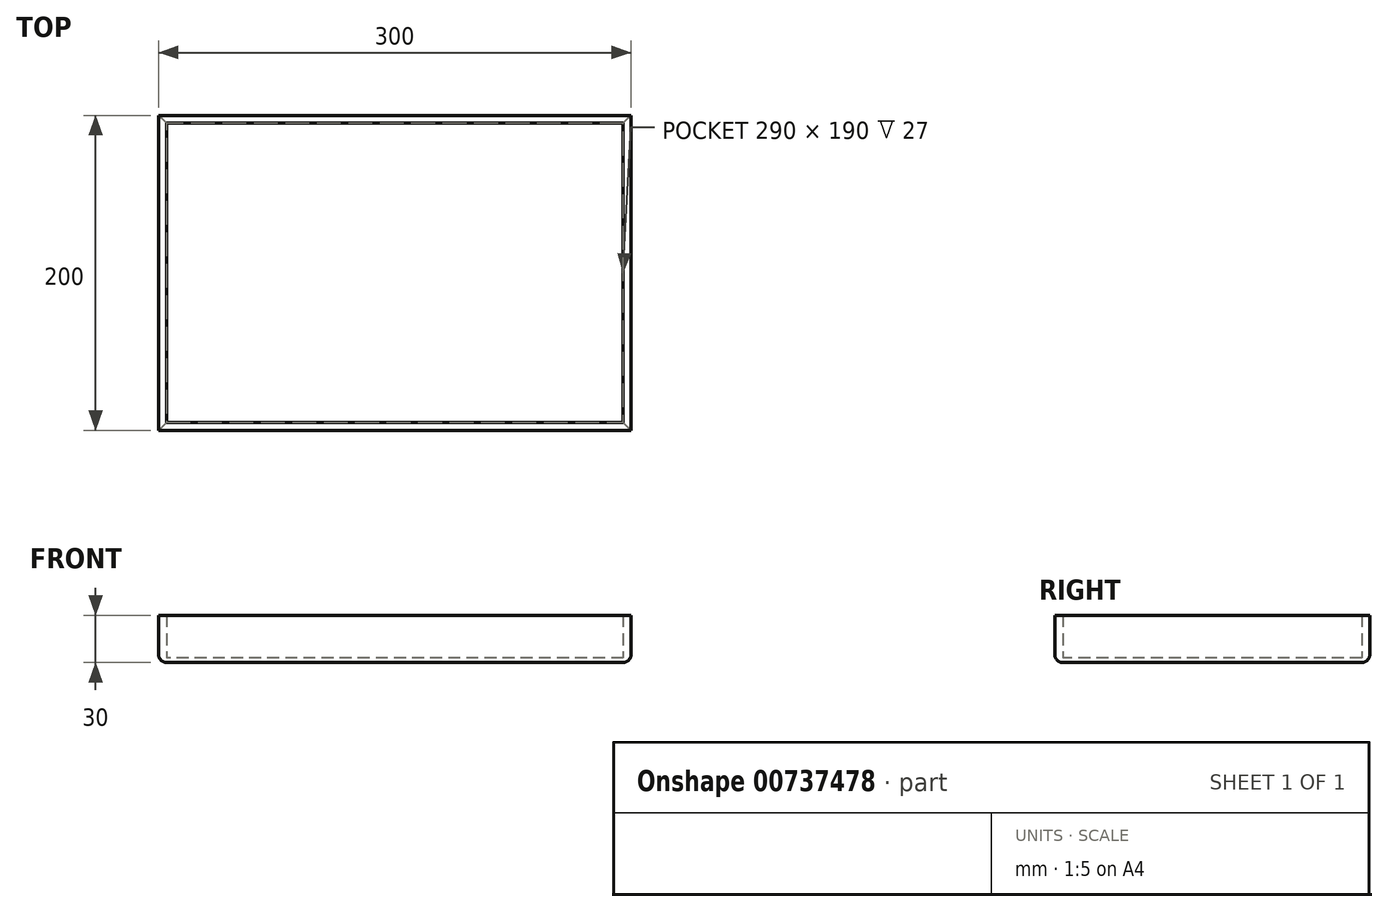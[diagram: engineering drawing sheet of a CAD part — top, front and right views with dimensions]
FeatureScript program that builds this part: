
annotation { "Feature Type Name" : "Feature", "Feature Type Description" : "" }
export const myFeature = defineFeature(function(context is Context, id is Id, definition is map)
    precondition{}
    {
        {
            var Q0;
            Q0=qCreatedBy(makeId("Top.planeOp"),FACE);
            var sketch = newSketch(context, id + "F0", { "sketchPlane" : qUnion([Q0])});
            skLineSegment(sketch, "E0.bottom", {"start": v(150, 100) * mm, "end": v(-150, 100) * mm});
            skLineSegment(sketch, "E0.top", {"start": v(150, -100) * mm, "end": v(-150, -100) * mm});
            skLineSegment(sketch, "E0.left", {"start": v(150, 100) * mm, "end": v(150, -100) * mm});
            skLineSegment(sketch, "E0.right", {"start": v(-150, 100) * mm, "end": v(-150, -100) * mm});
            skPoint(sketch, "E0.middle", {"position": v(0, 0) * mm});
            skLineSegment(sketch, "E1.bottom", {"start": v(145, 95) * mm, "end": v(-145, 95) * mm});
            skLineSegment(sketch, "E1.top", {"start": v(145, -95) * mm, "end": v(-145, -95) * mm});
            skLineSegment(sketch, "E1.left", {"start": v(145, 95) * mm, "end": v(145, -95) * mm});
            skLineSegment(sketch, "E1.right", {"start": v(-145, 95) * mm, "end": v(-145, -95) * mm});
            skLineSegment(sketch, "E2.bottom", {"start": v(147.5, 97.5) * mm, "end": v(-147.5, 97.5) * mm});
            skLineSegment(sketch, "E2.top", {"start": v(147.5, -97.5) * mm, "end": v(-147.5, -97.5) * mm});
            skLineSegment(sketch, "E2.left", {"start": v(147.5, 97.5) * mm, "end": v(147.5, -97.5) * mm});
            skLineSegment(sketch, "E2.right", {"start": v(-147.5, 97.5) * mm, "end": v(-147.5, -97.5) * mm});
            skSolve(sketch);
        }
        {
            var Q0;
            Q0=makeQuery(id+"F0.imprint","IMPRINT",FACE,{"disambiguationData":[TD([[makeQuery(id+"F0.imprint","IMPRINT",EDGE,{"derivedFrom":sQuery(id+"F0.wireOp",EDGE,"E0.bottom")}),1.0]])]});
            var Q1;
            Q1=makeQuery(id+"F0.imprint","IMPRINT",FACE,{"disambiguationData":[TD([[makeQuery(id+"F0.imprint","IMPRINT",EDGE,{"derivedFrom":sQuery(id+"F0.wireOp",EDGE,"E1.bottom")}),-1.0]])]});
            extrude(context, id + "F1", {"entities" : qUnion([Q0, Q1]), "depth" : 30 * mm, "offsetDistance" : 25 * mm});
        }
        {
            var Q0;
            Q0=makeQuery(id+"F0.imprint","IMPRINT",FACE,{"disambiguationData":[TD([[makeQuery(id+"F0.imprint","IMPRINT",EDGE,{"derivedFrom":sQuery(id+"F0.wireOp",EDGE,"E1.bottom")}),-1.0]])]});
            extrude(context, id + "F2", {"entities" : qUnion([Q0]), "operationType" : NewBodyOperationType.REMOVE, "depth" : 3 * mm, "offsetDistance" : 25 * mm});
        }
        {
            var Q0;
            Q0=makeQuery(id+"F0.imprint","IMPRINT",FACE,{"disambiguationData":[TD([[makeQuery(id+"F0.imprint","IMPRINT",EDGE,{"derivedFrom":sQuery(id+"F0.wireOp",EDGE,"E1.bottom")}),-1.0]])]});
            var Q1;
            Q1=makeQuery(id+"F0.imprint","IMPRINT",FACE,{"disambiguationData":[TD([[makeQuery(id+"F0.imprint","IMPRINT",EDGE,{"derivedFrom":sQuery(id+"F0.wireOp",EDGE,"E1.bottom")}),1.0]])]});
            extrude(context, id + "F3", {"entities" : qUnion([Q0, Q1]), "operationType" : NewBodyOperationType.ADD, "depth" : 3 * mm, "offsetDistance" : 25 * mm});
        }
        {
            var Q0;
            Q0=makeQuery(id+"F3.boolean.opBoolean","MERGE",FACE,{"derivedFrom":[makeQuery(id+"F1.opExtrude","CAP_FACE",FACE,{"disambiguationData":[OSD([sQuery(id+"F0.wireOp",EDGE,"E0.bottom"),sQuery(id+"F0.wireOp",EDGE,"E0.top"),sQuery(id+"F0.wireOp",EDGE,"E0.left"),sQuery(id+"F0.wireOp",EDGE,"E0.right"),sQuery(id+"F0.wireOp",EDGE,"E1.bottom"),sQuery(id+"F0.wireOp",EDGE,"E1.top"),sQuery(id+"F0.wireOp",EDGE,"E1.left"),sQuery(id+"F0.wireOp",EDGE,"E1.right")])],"isStart":true}),makeQuery(id+"F3.opExtrude","CAP_FACE",FACE,{"disambiguationData":[OSD([sQuery(id+"F0.wireOp",EDGE,"E2.bottom"),sQuery(id+"F0.wireOp",EDGE,"E2.top"),sQuery(id+"F0.wireOp",EDGE,"E2.left"),sQuery(id+"F0.wireOp",EDGE,"E2.right")])],"isStart":true})]});
            fillet(context, id + "F4", {"entities" : qUnion([Q0]), "radius" : 5 * mm, "tangentPropagation" : true, "allowEdgeOverflow" : false});
        }
    });
